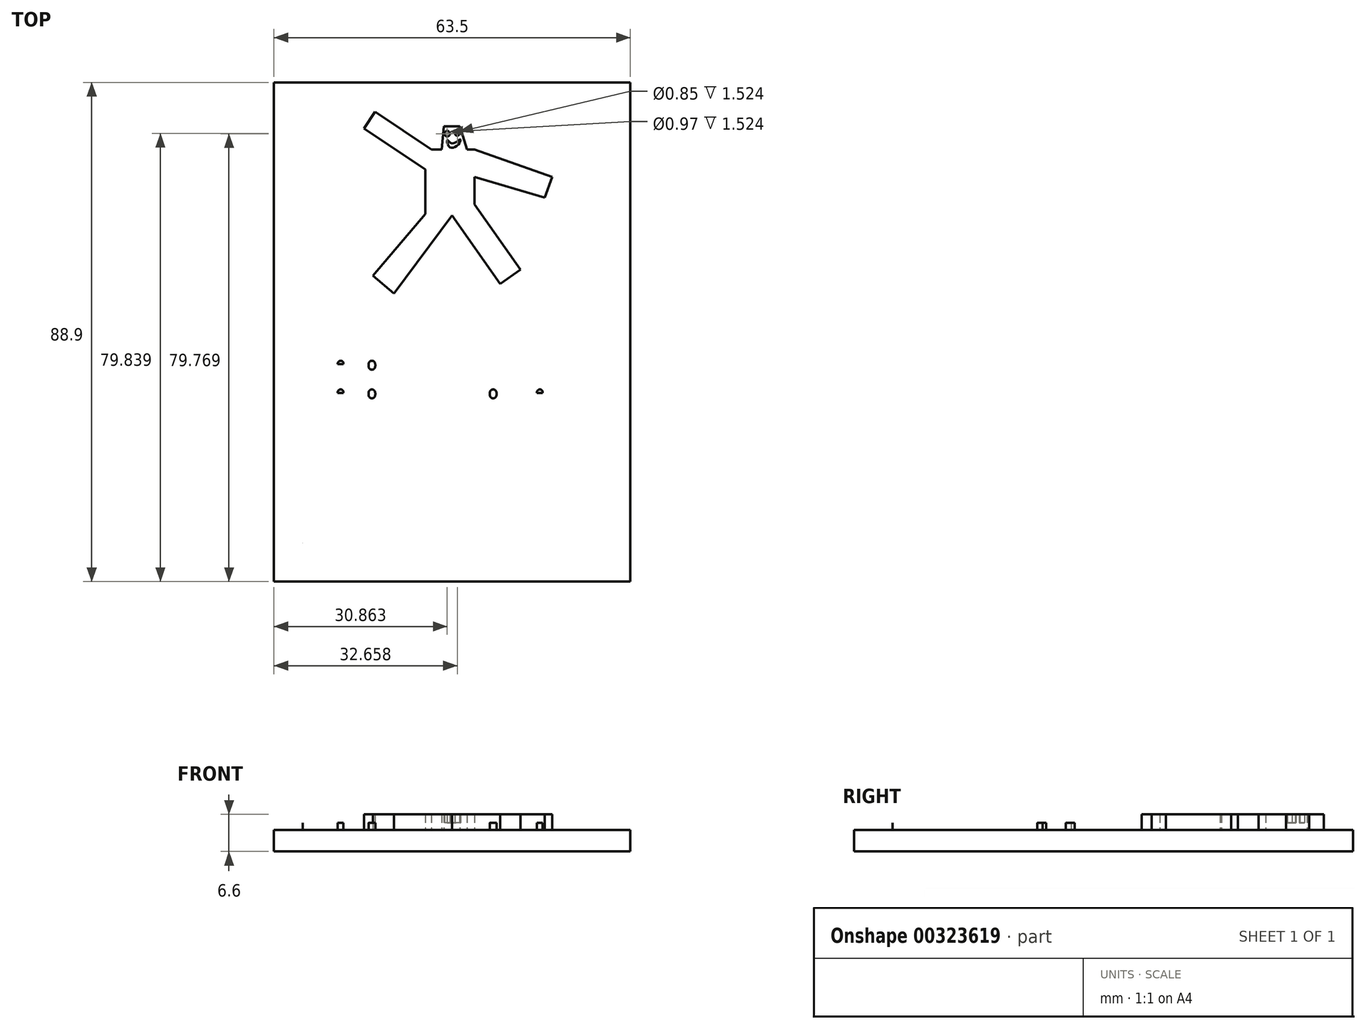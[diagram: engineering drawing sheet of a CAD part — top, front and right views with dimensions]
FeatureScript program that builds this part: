
annotation { "Feature Type Name" : "Feature", "Feature Type Description" : "" }
export const myFeature = defineFeature(function(context is Context, id is Id, definition is map)
    precondition{}
    {
        {
            var Q0;
            Q0=qCreatedBy(makeId("Top.planeOp"),FACE);
            var sketch = newSketch(context, id + "F0", { "sketchPlane" : qUnion([Q0])});
            skLineSegment(sketch, "E0.bottom", {"start": v(31.75, -44.45) * mm, "end": v(-31.75, -44.45) * mm});
            skLineSegment(sketch, "E0.top", {"start": v(31.75, 44.45) * mm, "end": v(-31.75, 44.45) * mm});
            skLineSegment(sketch, "E0.left", {"start": v(31.75, -44.45) * mm, "end": v(31.75, 44.45) * mm});
            skLineSegment(sketch, "E0.right", {"start": v(-31.75, -44.45) * mm, "end": v(-31.75, 44.45) * mm});
            skPoint(sketch, "E0.middle", {"position": v(0, 0) * mm});
            skSolve(sketch);
        }
        {
            var Q0;
            Q0=makeQuery(id+"F0.imprint","IMPRINT",FACE,{"disambiguationData":[TD([[makeQuery(id+"F0.imprint","IMPRINT",EDGE,{"derivedFrom":sQuery(id+"F0.wireOp",EDGE,"E0.bottom")}),-1.0]])]});
            extrude(context, id + "F1", {"entities" : qUnion([Q0]), "depth" : 5.08 * mm});
        }
        {
            var Q0;
            Q0=makeQuery(id+"F1.opExtrude","CAP_FACE",FACE,{"disambiguationData":[OSD([sQuery(id+"F0.wireOp",EDGE,"E0.bottom"),sQuery(id+"F0.wireOp",EDGE,"E0.top"),sQuery(id+"F0.wireOp",EDGE,"E0.left"),sQuery(id+"F0.wireOp",EDGE,"E0.right")])],"isStart":false});
            var sketch = newSketch(context, id + "F2", { "sketchPlane" : qUnion([Q0])});
            skLineSegment(sketch, "E1", {"start": v(0, 20.73) * mm, "end": v(8.52, 8.58) * mm});
            skLineSegment(sketch, "E2", {"start": v(8.52, 8.58) * mm, "end": v(12.15, 11.12) * mm});
            skLineSegment(sketch, "E3", {"start": v(12.15, 11.12) * mm, "end": v(4, 22.73) * mm});
            skLineSegment(sketch, "E4", {"start": v(4, 22.73) * mm, "end": v(4, 32.53) * mm});
            skLineSegment(sketch, "E5", {"start": v(4, 32.53) * mm, "end": v(0, 32.53) * mm});
            skLineSegment(sketch, "E6", {"start": v(0, 32.53) * mm, "end": v(-3.7, 32.53) * mm});
            skLineSegment(sketch, "E7", {"start": v(-3.7, 32.53) * mm, "end": v(-13.72, 39.26) * mm});
            skLineSegment(sketch, "E8", {"start": v(-13.72, 39.26) * mm, "end": v(-15.73, 36.26) * mm});
            skLineSegment(sketch, "E9", {"start": v(-15.73, 36.26) * mm, "end": v(-4.8, 28.92) * mm});
            skLineSegment(sketch, "E10", {"start": v(-4.8, 28.92) * mm, "end": v(-4.8, 21) * mm});
            skLineSegment(sketch, "E11", {"start": v(-4.8, 21) * mm, "end": v(-14.13, 10.02) * mm});
            skLineSegment(sketch, "E12", {"start": v(-14.13, 10.02) * mm, "end": v(-10.37, 6.82) * mm});
            skLineSegment(sketch, "E13", {"start": v(-10.37, 6.82) * mm, "end": v(0, 20.73) * mm});
            skLineSegment(sketch, "E14", {"start": v(4, 32.53) * mm, "end": v(17.8, 27.63) * mm});
            skPoint(sketch, "E14.endSnap0", {"position": v(4, 27.63) * mm});
            skLineSegment(sketch, "E15", {"start": v(17.8, 27.63) * mm, "end": v(16.49, 23.96) * mm});
            skLineSegment(sketch, "E16", {"start": v(16.49, 23.96) * mm, "end": v(4, 27.63) * mm});
            skLineSegment(sketch, "E17", {"start": v(-1.85, 32.53) * mm, "end": v(-1.48, 36.6) * mm});
            skLineSegment(sketch, "E18", {"start": v(-1.48, 36.6) * mm, "end": v(0, 36.6) * mm});
            skLineSegment(sketch, "E19", {"start": v(0, 36.6) * mm, "end": v(1.4, 36.6) * mm});
            skLineSegment(sketch, "E20", {"start": v(1.4, 36.6) * mm, "end": v(2.62, 32.53) * mm});
            skCircle(sketch, "E21", {"center": v(-0.89, 35.32) * mm, "radius": 0.48 * mm});
            skCircle(sketch, "E22", {"center": v(0.9, 35.39) * mm, "radius": 0.42 * mm});
            skFitSpline(sketch, "E23", {"points": [v(-0.85, 34.16) * mm, v(0, 33.57) * mm, v(1.45, 34.3) * mm, v(0.9, 33.2) * mm, v(-0.56, 33.01) * mm, v(-0.85, 34.16) * mm]});
            skText(sketch, "E24", { "text": "servo, jimmy:\nservo jimmy is worthless.    \n                                            1/1", "fontName": "OpenSans-Regular.ttf"});
            const initialGuessF2  = {"E24": [-0.02274, -0.00693, 1, 0, 0.0027]};
            skSetInitialGuess(sketch, initialGuessF2);
            skSolve(sketch);
        }
        {
            var Q0;
            Q0=makeQuery(id+"F2.imprint","IMPRINT",FACE,{"disambiguationData":[TD([[makeQuery(id+"F2.imprint","IMPRINT",EDGE,{"derivedFrom":sQuery(id+"F2.wireOp",EDGE,"E24.sketch_text.stroke-0")}),-1.0]])]});
            var Q1;
            Q1=makeQuery(id+"F2.imprint","IMPRINT",FACE,{"disambiguationData":[TD([[makeQuery(id+"F2.imprint","IMPRINT",EDGE,{"derivedFrom":sQuery(id+"F2.wireOp",EDGE,"E24.sketch_text.stroke-25")}),-1.0]])]});
            var Q2;
            Q2=makeQuery(id+"F2.imprint","IMPRINT",FACE,{"disambiguationData":[TD([[makeQuery(id+"F2.imprint","IMPRINT",EDGE,{"derivedFrom":sQuery(id+"F2.wireOp",EDGE,"E24.sketch_text.stroke-44")}),-1.0]])]});
            var Q3;
            Q3=makeQuery(id+"F2.imprint","IMPRINT",FACE,{"disambiguationData":[TD([[makeQuery(id+"F2.imprint","IMPRINT",EDGE,{"derivedFrom":sQuery(id+"F2.wireOp",EDGE,"E24.sketch_text.stroke-57")}),-1.0]])]});
            var Q4;
            Q4=makeQuery(id+"F2.imprint","IMPRINT",FACE,{"disambiguationData":[TD([[makeQuery(id+"F2.imprint","IMPRINT",EDGE,{"derivedFrom":sQuery(id+"F2.wireOp",EDGE,"E24.sketch_text.stroke-67")}),-1.0]])]});
            var Q5;
            Q5=makeQuery(id+"F2.imprint","IMPRINT",FACE,{"disambiguationData":[TD([[makeQuery(id+"F2.imprint","IMPRINT",EDGE,{"derivedFrom":sQuery(id+"F2.wireOp",EDGE,"E24.sketch_text.stroke-84")}),-1.0]])]});
            var Q6;
            Q6=makeQuery(id+"F2.imprint","IMPRINT",FACE,{"disambiguationData":[TD([[makeQuery(id+"F2.imprint","IMPRINT",EDGE,{"derivedFrom":sQuery(id+"F2.wireOp",EDGE,"E24.sketch_text.stroke-91")}),-1.0]])]});
            var Q7;
            Q7=makeQuery(id+"F2.imprint","IMPRINT",FACE,{"disambiguationData":[TD([[makeQuery(id+"F2.imprint","IMPRINT",EDGE,{"derivedFrom":sQuery(id+"F2.wireOp",EDGE,"E24.sketch_text.stroke-100")}),-1.0]])]});
            var Q8;
            Q8=makeQuery(id+"F2.imprint","IMPRINT",FACE,{"disambiguationData":[TD([[makeQuery(id+"F2.imprint","IMPRINT",EDGE,{"derivedFrom":sQuery(id+"F2.wireOp",EDGE,"E24.sketch_text.stroke-112")}),-1.0]])]});
            var Q9;
            Q9=makeQuery(id+"F2.imprint","IMPRINT",FACE,{"disambiguationData":[TD([[makeQuery(id+"F2.imprint","IMPRINT",EDGE,{"derivedFrom":sQuery(id+"F2.wireOp",EDGE,"E24.sketch_text.stroke-108")}),-1.0]])]});
            var Q10;
            Q10=makeQuery(id+"F2.imprint","IMPRINT",FACE,{"disambiguationData":[TD([[makeQuery(id+"F2.imprint","IMPRINT",EDGE,{"derivedFrom":sQuery(id+"F2.wireOp",EDGE,"E24.sketch_text.stroke-120")}),-1.0]])]});
            var Q11;
            Q11=makeQuery(id+"F2.imprint","IMPRINT",FACE,{"disambiguationData":[TD([[makeQuery(id+"F2.imprint","IMPRINT",EDGE,{"derivedFrom":sQuery(id+"F2.wireOp",EDGE,"E24.sketch_text.stroke-148")}),-1.0]])]});
            var Q12;
            Q12=makeQuery(id+"F2.imprint","IMPRINT",FACE,{"disambiguationData":[TD([[makeQuery(id+"F2.imprint","IMPRINT",EDGE,{"derivedFrom":sQuery(id+"F2.wireOp",EDGE,"E24.sketch_text.stroke-176")}),-1.0]])]});
            var Q13;
            Q13=makeQuery(id+"F2.imprint","IMPRINT",FACE,{"disambiguationData":[TD([[makeQuery(id+"F2.imprint","IMPRINT",EDGE,{"derivedFrom":sQuery(id+"F2.wireOp",EDGE,"E24.sketch_text.stroke-200")}),-1.0]])]});
            var Q14;
            Q14=makeQuery(id+"F2.imprint","IMPRINT",FACE,{"disambiguationData":[TD([[makeQuery(id+"F2.imprint","IMPRINT",EDGE,{"derivedFrom":sQuery(id+"F2.wireOp",EDGE,"E24.sketch_text.stroke-192")}),-1.0]])]});
            var Q15;
            Q15=makeQuery(id+"F2.imprint","IMPRINT",FACE,{"disambiguationData":[TD([[makeQuery(id+"F2.imprint","IMPRINT",EDGE,{"derivedFrom":sQuery(id+"F2.wireOp",EDGE,"E24.sketch_text.stroke-206")}),-1.0]])]});
            var Q16;
            Q16=makeQuery(id+"F2.imprint","IMPRINT",FACE,{"disambiguationData":[TD([[makeQuery(id+"F2.imprint","IMPRINT",EDGE,{"derivedFrom":sQuery(id+"F2.wireOp",EDGE,"E24.sketch_text.stroke-231")}),-1.0]])]});
            var Q17;
            Q17=makeQuery(id+"F2.imprint","IMPRINT",FACE,{"disambiguationData":[TD([[makeQuery(id+"F2.imprint","IMPRINT",EDGE,{"derivedFrom":sQuery(id+"F2.wireOp",EDGE,"E24.sketch_text.stroke-250")}),-1.0]])]});
            var Q18;
            Q18=makeQuery(id+"F2.imprint","IMPRINT",FACE,{"disambiguationData":[TD([[makeQuery(id+"F2.imprint","IMPRINT",EDGE,{"derivedFrom":sQuery(id+"F2.wireOp",EDGE,"E24.sketch_text.stroke-263")}),-1.0]])]});
            var Q19;
            Q19=makeQuery(id+"F2.imprint","IMPRINT",FACE,{"disambiguationData":[TD([[makeQuery(id+"F2.imprint","IMPRINT",EDGE,{"derivedFrom":sQuery(id+"F2.wireOp",EDGE,"E24.sketch_text.stroke-273")}),-1.0]])]});
            var Q20;
            Q20=makeQuery(id+"F2.imprint","IMPRINT",FACE,{"disambiguationData":[TD([[makeQuery(id+"F2.imprint","IMPRINT",EDGE,{"derivedFrom":sQuery(id+"F2.wireOp",EDGE,"E24.sketch_text.stroke-290")}),-1.0]])]});
            var Q21;
            Q21=makeQuery(id+"F2.imprint","IMPRINT",FACE,{"disambiguationData":[TD([[makeQuery(id+"F2.imprint","IMPRINT",EDGE,{"derivedFrom":sQuery(id+"F2.wireOp",EDGE,"E24.sketch_text.stroke-311")}),-1.0]])]});
            var Q22;
            Q22=makeQuery(id+"F2.imprint","IMPRINT",FACE,{"disambiguationData":[TD([[makeQuery(id+"F2.imprint","IMPRINT",EDGE,{"derivedFrom":sQuery(id+"F2.wireOp",EDGE,"E24.sketch_text.stroke-299")}),-1.0]])]});
            var Q23;
            Q23=makeQuery(id+"F2.imprint","IMPRINT",FACE,{"disambiguationData":[TD([[makeQuery(id+"F2.imprint","IMPRINT",EDGE,{"derivedFrom":sQuery(id+"F2.wireOp",EDGE,"E24.sketch_text.stroke-319")}),-1.0]])]});
            var Q24;
            Q24=makeQuery(id+"F2.imprint","IMPRINT",FACE,{"disambiguationData":[TD([[makeQuery(id+"F2.imprint","IMPRINT",EDGE,{"derivedFrom":sQuery(id+"F2.wireOp",EDGE,"E24.sketch_text.stroke-307")}),-1.0]])]});
            var Q25;
            Q25=makeQuery(id+"F2.imprint","IMPRINT",FACE,{"disambiguationData":[TD([[makeQuery(id+"F2.imprint","IMPRINT",EDGE,{"derivedFrom":sQuery(id+"F2.wireOp",EDGE,"E24.sketch_text.stroke-395")}),-1.0]])]});
            var Q26;
            Q26=makeQuery(id+"F2.imprint","IMPRINT",FACE,{"disambiguationData":[TD([[makeQuery(id+"F2.imprint","IMPRINT",EDGE,{"derivedFrom":sQuery(id+"F2.wireOp",EDGE,"E24.sketch_text.stroke-403")}),-1.0]])]});
            var Q27;
            Q27=makeQuery(id+"F2.imprint","IMPRINT",FACE,{"disambiguationData":[TD([[makeQuery(id+"F2.imprint","IMPRINT",EDGE,{"derivedFrom":sQuery(id+"F2.wireOp",EDGE,"E24.sketch_text.stroke-391")}),-1.0]])]});
            var Q28;
            Q28=makeQuery(id+"F2.imprint","IMPRINT",FACE,{"disambiguationData":[TD([[makeQuery(id+"F2.imprint","IMPRINT",EDGE,{"derivedFrom":sQuery(id+"F2.wireOp",EDGE,"E24.sketch_text.stroke-347")}),-1.0]])]});
            var Q29;
            Q29=makeQuery(id+"F2.imprint","IMPRINT",FACE,{"disambiguationData":[TD([[makeQuery(id+"F2.imprint","IMPRINT",EDGE,{"derivedFrom":sQuery(id+"F2.wireOp",EDGE,"E24.sketch_text.stroke-375")}),-1.0]])]});
            var Q30;
            Q30=makeQuery(id+"F2.imprint","IMPRINT",FACE,{"disambiguationData":[TD([[makeQuery(id+"F2.imprint","IMPRINT",EDGE,{"derivedFrom":sQuery(id+"F2.wireOp",EDGE,"E24.sketch_text.stroke-451")}),-1.0]])]});
            var Q31;
            Q31=makeQuery(id+"F2.imprint","IMPRINT",FACE,{"disambiguationData":[TD([[makeQuery(id+"F2.imprint","IMPRINT",EDGE,{"derivedFrom":sQuery(id+"F2.wireOp",EDGE,"E24.sketch_text.stroke-428")}),-1.0]])]});
            var Q32;
            Q32=makeQuery(id+"F2.imprint","IMPRINT",FACE,{"disambiguationData":[TD([[makeQuery(id+"F2.imprint","IMPRINT",EDGE,{"derivedFrom":sQuery(id+"F2.wireOp",EDGE,"E24.sketch_text.stroke-468")}),-1.0]])]});
            var Q33;
            Q33=makeQuery(id+"F2.imprint","IMPRINT",FACE,{"disambiguationData":[TD([[makeQuery(id+"F2.imprint","IMPRINT",EDGE,{"derivedFrom":sQuery(id+"F2.wireOp",EDGE,"E24.sketch_text.stroke-481")}),-1.0]])]});
            var Q34;
            Q34=makeQuery(id+"F2.imprint","IMPRINT",FACE,{"disambiguationData":[TD([[makeQuery(id+"F2.imprint","IMPRINT",EDGE,{"derivedFrom":sQuery(id+"F2.wireOp",EDGE,"E24.sketch_text.stroke-500")}),-1.0]])]});
            var Q35;
            Q35=makeQuery(id+"F2.imprint","IMPRINT",FACE,{"disambiguationData":[TD([[makeQuery(id+"F2.imprint","IMPRINT",EDGE,{"derivedFrom":sQuery(id+"F2.wireOp",EDGE,"E24.sketch_text.stroke-518")}),-1.0]])]});
            var Q36;
            Q36=makeQuery(id+"F2.imprint","IMPRINT",FACE,{"disambiguationData":[TD([[makeQuery(id+"F2.imprint","IMPRINT",EDGE,{"derivedFrom":sQuery(id+"F2.wireOp",EDGE,"E24.sketch_text.stroke-522")}),-1.0]])]});
            var Q37;
            Q37=makeQuery(id+"F2.imprint","IMPRINT",FACE,{"disambiguationData":[TD([[makeQuery(id+"F2.imprint","IMPRINT",EDGE,{"derivedFrom":sQuery(id+"F2.wireOp",EDGE,"E24.sketch_text.stroke-541")}),-1.0]])]});
            var Q38;
            Q38=makeQuery(id+"F2.imprint","IMPRINT",FACE,{"disambiguationData":[TD([[makeQuery(id+"F2.imprint","IMPRINT",EDGE,{"derivedFrom":sQuery(id+"F2.wireOp",EDGE,"E24.sketch_text.stroke-566")}),-1.0]])]});
            var Q39;
            Q39=makeQuery(id+"F2.imprint","IMPRINT",FACE,{"disambiguationData":[TD([[makeQuery(id+"F2.imprint","IMPRINT",EDGE,{"derivedFrom":sQuery(id+"F2.wireOp",EDGE,"E24.sketch_text.stroke-599")}),-1.0]])]});
            var Q40;
            Q40=makeQuery(id+"F2.imprint","IMPRINT",FACE,{"disambiguationData":[TD([[makeQuery(id+"F2.imprint","IMPRINT",EDGE,{"derivedFrom":sQuery(id+"F2.wireOp",EDGE,"E24.sketch_text.stroke-608")}),-1.0]])]});
            var Q41;
            Q41=makeQuery(id+"F2.imprint","IMPRINT",FACE,{"disambiguationData":[TD([[makeQuery(id+"F2.imprint","IMPRINT",EDGE,{"derivedFrom":sQuery(id+"F2.wireOp",EDGE,"E24.sketch_text.stroke-612")}),-1.0]])]});
            var Q42;
            Q42=makeQuery(id+"F2.imprint","IMPRINT",FACE,{"disambiguationData":[TD([[makeQuery(id+"F2.imprint","IMPRINT",EDGE,{"derivedFrom":sQuery(id+"F2.wireOp",EDGE,"E24.sketch_text.stroke-591")}),-1.0]])]});
            extrude(context, id + "F3", {"entities" : qUnion([Q0, Q1, Q2, Q3, Q4, Q5, Q6, Q7, Q8, Q9, Q10, Q11, Q12, Q13, Q14, Q15, Q16, Q17, Q18, Q19, Q20, Q21, Q22, Q23, Q24, Q25, Q26, Q27, Q28, Q29, Q30, Q31, Q32, Q33, Q34, Q35, Q36, Q37, Q38, Q39, Q40, Q41, Q42]), "operationType" : NewBodyOperationType.REMOVE, "oppositeDirection" : true, "depth" : 1.27 * mm});
        }
        {
            var Q0;
            Q0=makeQuery(id+"F2.imprint","IMPRINT",FACE,{"disambiguationData":[TD([[makeQuery(id+"F2.imprint","IMPRINT",EDGE,{"derivedFrom":sQuery(id+"F2.wireOp",EDGE,"E1")}),1.0]])]});
            var Q1;
            {var subQ0=sQuery(id+"F2.wireOp",EDGE,"E14");Q1=makeQuery(id+"F2.imprint","IMPRINT",FACE,{"disambiguationData":[TD([[makeQuery(id+"F2.imprint","IMPRINT",EDGE,{"derivedFrom":subQ0}),-1.0]])]});}
            var Q2;
            {var subQ0=sQuery(id+"F2.wireOp",EDGE,"E17");Q2=makeQuery(id+"F2.imprint","IMPRINT",FACE,{"disambiguationData":[TD([[makeQuery(id+"F2.imprint","IMPRINT",EDGE,{"derivedFrom":subQ0}),-1.0]])]});}
            extrude(context, id + "F4", {"entities" : qUnion([Q0, Q1, Q2]), "operationType" : NewBodyOperationType.ADD, "depth" : 1.52 * mm});
        }
        {
            var Q0;
            Q0=makeQuery(id+"F2.imprint","IMPRINT",FACE,{"disambiguationData":[TD([[makeQuery(id+"F2.imprint","IMPRINT",EDGE,{"derivedFrom":sQuery(id+"F2.wireOp",EDGE,"E1")}),-1.0]])]});
            var sketch = newSketch(context, id + "F5", { "sketchPlane" : qUnion([Q0])});
            skFitSpline(sketch, "E25", {"points": [v(-26.28, -37.6) * mm, v(-24.66, -36.24) * mm, v(-26, -34.84) * mm, v(-27.95, -36.5) * mm, v(-26.28, -37.6) * mm]});
            skFitSpline(sketch, "E26", {"points": [v(-26.28, -37.6) * mm, v(-24.66, -37.6) * mm, v(-24.66, -38.83) * mm, v(-26.28, -39.8) * mm, v(-27.48, -38.6) * mm, v(-26.28, -37.6) * mm]});
            skLineSegment(sketch, "E27", {"start": v(-26.68, -33.27) * mm, "end": v(-25.12, -41.42) * mm});
            skLineSegment(sketch, "E28", {"start": v(-28.77, -38.13) * mm, "end": v(-22.3, -36.5) * mm});
            skLineSegment(sketch, "E29.bottom", {"start": v(-22.3, -37.31) * mm, "end": v(-30.26, -37.31) * mm});
            skLineSegment(sketch, "E29.top", {"start": v(-22.3, -37.89) * mm, "end": v(-30.26, -37.89) * mm});
            skLineSegment(sketch, "E29.left", {"start": v(-22.3, -37.31) * mm, "end": v(-22.3, -37.89) * mm});
            skLineSegment(sketch, "E29.right", {"start": v(-30.26, -37.31) * mm, "end": v(-30.26, -37.89) * mm});
            skPoint(sketch, "E29.cornerSnap0", {"position": v(-25.53, -37.31) * mm});
            skLineSegment(sketch, "E30.bottom", {"start": v(-25.9, -42.16) * mm, "end": v(-26.65, -42.16) * mm});
            skLineSegment(sketch, "E30.top", {"start": v(-25.9, -33.04) * mm, "end": v(-26.65, -33.04) * mm});
            skLineSegment(sketch, "E30.left", {"start": v(-25.9, -42.16) * mm, "end": v(-25.9, -33.04) * mm});
            skLineSegment(sketch, "E30.right", {"start": v(-26.65, -42.16) * mm, "end": v(-26.65, -33.04) * mm});
            skPoint(sketch, "E30.cornerSnap0", {"position": v(-25.9, -37.34) * mm});
            skSolve(sketch);
        }
        {
            var Q0;
            {var subQ0=sQuery(id+"F5.wireOp",EDGE,"E29.left");Q0=makeQuery(id+"F5.imprint","IMPRINT",FACE,{"disambiguationData":[TD([[makeQuery(id+"F5.imprint","IMPRINT",EDGE,{"derivedFrom":subQ0}),-1.0]])]});}
            var Q1;
            {var subQ0=sQuery(id+"F5.wireOp",EDGE,"E29.right");Q1=makeQuery(id+"F5.imprint","IMPRINT",FACE,{"disambiguationData":[TD([[makeQuery(id+"F5.imprint","IMPRINT",EDGE,{"derivedFrom":subQ0}),1.0]])]});}
            var Q2;
            {var subQ0=sQuery(id+"F5.wireOp",EDGE,"E27");var subQ1=sQuery(id+"F5.wireOp",EDGE,"E25");var subQ2=makeQuery(id+"F5.imprint","INTERSECT",VERTEX,{"disambiguationData":[OD(0.0)],"derivedFrom":[subQ1,subQ0]});Q2=makeQuery(id+"F5.imprint","IMPRINT",FACE,{"disambiguationData":[TD([[makeQuery(id+"F5.imprint","IMPRINT",EDGE,{"disambiguationData":[TD([[subQ2,-1.0]])],"derivedFrom":subQ1}),-1.0]])]});}
            var Q3;
            {var subQ0=sQuery(id+"F5.wireOp",EDGE,"E30.left");var subQ1=sQuery(id+"F5.wireOp",EDGE,"E25");var subQ2=makeQuery(id+"F5.imprint","INTERSECT",VERTEX,{"disambiguationData":[OD(0.0)],"derivedFrom":[subQ1,subQ0]});Q3=makeQuery(id+"F5.imprint","IMPRINT",FACE,{"disambiguationData":[TD([[makeQuery(id+"F5.imprint","IMPRINT",EDGE,{"disambiguationData":[TD([[subQ2,1.0]])],"derivedFrom":subQ1}),-1.0]])]});}
            var Q4;
            {var subQ0=sQuery(id+"F5.wireOp",EDGE,"E30.left");var subQ1=sQuery(id+"F5.wireOp",EDGE,"E25");var subQ2=makeQuery(id+"F5.imprint","INTERSECT",VERTEX,{"disambiguationData":[OD(0.0)],"derivedFrom":[subQ1,subQ0]});Q4=makeQuery(id+"F5.imprint","IMPRINT",FACE,{"disambiguationData":[TD([[makeQuery(id+"F5.imprint","IMPRINT",EDGE,{"disambiguationData":[TD([[subQ2,-1.0]])],"derivedFrom":subQ1}),-1.0]])]});}
            var Q5;
            {var subQ0=sQuery(id+"F5.wireOp",EDGE,"E29.top");var subQ1=sQuery(id+"F5.wireOp",EDGE,"E26");var subQ2=makeQuery(id+"F5.imprint","INTERSECT",VERTEX,{"disambiguationData":[OD(1.0)],"derivedFrom":[subQ1,subQ0]});Q5=makeQuery(id+"F5.imprint","IMPRINT",FACE,{"disambiguationData":[TD([[makeQuery(id+"F5.imprint","IMPRINT",EDGE,{"disambiguationData":[TD([[subQ2,-1.0]])],"derivedFrom":subQ1}),-1.0]])]});}
            var Q6;
            {var subQ0=sQuery(id+"F5.wireOp",EDGE,"E29.top");var subQ1=sQuery(id+"F5.wireOp",EDGE,"E26");var subQ2=makeQuery(id+"F5.imprint","INTERSECT",VERTEX,{"disambiguationData":[OD(1.0)],"derivedFrom":[subQ1,subQ0]});Q6=makeQuery(id+"F5.imprint","IMPRINT",FACE,{"disambiguationData":[TD([[makeQuery(id+"F5.imprint","IMPRINT",EDGE,{"disambiguationData":[TD([[subQ2,-1.0]])],"derivedFrom":subQ1}),1.0]])]});}
            var Q7;
            {var subQ0=sQuery(id+"F5.wireOp",EDGE,"E26");var subQ1=sQuery(id+"F5.wireOp",EDGE,"E25");var subQ2=makeQuery(id+"F5.imprint","INTERSECT",VERTEX,{"disambiguationData":[OD(0.0)],"derivedFrom":[subQ1,subQ0]});Q7=makeQuery(id+"F5.imprint","IMPRINT",FACE,{"disambiguationData":[TD([[makeQuery(id+"F5.imprint","IMPRINT",EDGE,{"disambiguationData":[TD([[subQ2,1.0]])],"derivedFrom":subQ1}),-1.0]])]});}
            var Q8;
            {var subQ0=sQuery(id+"F5.wireOp",EDGE,"E26");var subQ1=sQuery(id+"F5.wireOp",EDGE,"E25");var subQ2=makeQuery(id+"F5.imprint","INTERSECT",VERTEX,{"disambiguationData":[OD(0.0)],"derivedFrom":[subQ1,subQ0]});Q8=makeQuery(id+"F5.imprint","IMPRINT",FACE,{"disambiguationData":[TD([[makeQuery(id+"F5.imprint","IMPRINT",EDGE,{"disambiguationData":[TD([[subQ2,1.0]])],"derivedFrom":subQ1}),1.0]])]});}
            var Q9;
            {var subQ0=sQuery(id+"F5.wireOp",EDGE,"E30.left");var subQ1=sQuery(id+"F5.wireOp",EDGE,"E25");var subQ2=makeQuery(id+"F5.imprint","INTERSECT",VERTEX,{"disambiguationData":[OD(0.0)],"derivedFrom":[subQ1,subQ0]});Q9=makeQuery(id+"F5.imprint","IMPRINT",FACE,{"disambiguationData":[TD([[makeQuery(id+"F5.imprint","IMPRINT",EDGE,{"disambiguationData":[TD([[subQ2,1.0]])],"derivedFrom":subQ1}),1.0]])]});}
            var Q10;
            {var subQ1=sQuery(id+"F5.wireOp",EDGE,"E26");var subQ6=sQuery(id+"F5.wireOp",EDGE,"E25");var subQ9=makeQuery(id+"F5.imprint","INTERSECT",VERTEX,{"disambiguationData":[OD(1.0)],"derivedFrom":[subQ6,subQ1]});Q10=makeQuery(id+"F5.imprint","IMPRINT",FACE,{"disambiguationData":[TD([[makeQuery(id+"F5.imprint","IMPRINT",EDGE,{"disambiguationData":[TD([[subQ9,-1.0]])],"derivedFrom":subQ6}),1.0]])]});}
            var Q11;
            {var subQ0=sQuery(id+"F5.wireOp",EDGE,"E30.left");var subQ1=sQuery(id+"F5.wireOp",EDGE,"E26");var subQ2=makeQuery(id+"F5.imprint","INTERSECT",VERTEX,{"disambiguationData":[OD(0.0)],"derivedFrom":[subQ1,subQ0]});Q11=makeQuery(id+"F5.imprint","IMPRINT",FACE,{"disambiguationData":[TD([[makeQuery(id+"F5.imprint","IMPRINT",EDGE,{"disambiguationData":[TD([[subQ2,-1.0]])],"derivedFrom":subQ1}),1.0]])]});}
            var Q12;
            {var subQ0=sQuery(id+"F5.wireOp",EDGE,"E27");var subQ1=sQuery(id+"F5.wireOp",EDGE,"E25");var subQ2=makeQuery(id+"F5.imprint","INTERSECT",VERTEX,{"disambiguationData":[OD(0.0)],"derivedFrom":[subQ1,subQ0]});Q12=makeQuery(id+"F5.imprint","IMPRINT",FACE,{"disambiguationData":[TD([[makeQuery(id+"F5.imprint","IMPRINT",EDGE,{"disambiguationData":[TD([[subQ2,-1.0]])],"derivedFrom":subQ1}),1.0]])]});}
            var Q13;
            {var subQ0=sQuery(id+"F5.wireOp",EDGE,"E30.left");var subQ1=sQuery(id+"F5.wireOp",EDGE,"E25");var subQ2=makeQuery(id+"F5.imprint","INTERSECT",VERTEX,{"disambiguationData":[OD(0.0)],"derivedFrom":[subQ1,subQ0]});Q13=makeQuery(id+"F5.imprint","IMPRINT",FACE,{"disambiguationData":[TD([[makeQuery(id+"F5.imprint","IMPRINT",EDGE,{"disambiguationData":[TD([[subQ2,-1.0]])],"derivedFrom":subQ1}),1.0]])]});}
            var Q14;
            {var subQ0=sQuery(id+"F5.wireOp",EDGE,"E29.bottom");var subQ1=sQuery(id+"F5.wireOp",EDGE,"E25");var subQ2=makeQuery(id+"F5.imprint","INTERSECT",VERTEX,{"disambiguationData":[OD(1.0)],"derivedFrom":[subQ1,subQ0]});Q14=makeQuery(id+"F5.imprint","IMPRINT",FACE,{"disambiguationData":[TD([[makeQuery(id+"F5.imprint","IMPRINT",EDGE,{"disambiguationData":[TD([[subQ2,-1.0]])],"derivedFrom":subQ1}),1.0]])]});}
            var Q15;
            {var subQ0=sQuery(id+"F5.wireOp",EDGE,"E30.right");var subQ1=sQuery(id+"F5.wireOp",EDGE,"E25");var subQ2=makeQuery(id+"F5.imprint","INTERSECT",VERTEX,{"disambiguationData":[OD(1.0)],"derivedFrom":[subQ1,subQ0]});Q15=makeQuery(id+"F5.imprint","IMPRINT",FACE,{"disambiguationData":[TD([[makeQuery(id+"F5.imprint","IMPRINT",EDGE,{"disambiguationData":[TD([[subQ2,-1.0]])],"derivedFrom":subQ1}),-1.0]])]});}
            var Q16;
            {var subQ0=sQuery(id+"F5.wireOp",EDGE,"E30.left");var subQ1=sQuery(id+"F5.wireOp",EDGE,"E27");var subQ2=makeQuery(id+"F5.imprint","INTERSECT",VERTEX,{"derivedFrom":[subQ1,subQ0]});Q16=makeQuery(id+"F5.imprint","IMPRINT",FACE,{"disambiguationData":[TD([[makeQuery(id+"F5.imprint","IMPRINT",EDGE,{"disambiguationData":[TD([[subQ2,-1.0]])],"derivedFrom":subQ1}),1.0]])]});}
            var Q17;
            {var subQ0=sQuery(id+"F5.wireOp",EDGE,"E30.left");var subQ1=sQuery(id+"F5.wireOp",EDGE,"E27");var subQ2=makeQuery(id+"F5.imprint","INTERSECT",VERTEX,{"derivedFrom":[subQ1,subQ0]});Q17=makeQuery(id+"F5.imprint","IMPRINT",FACE,{"disambiguationData":[TD([[makeQuery(id+"F5.imprint","IMPRINT",EDGE,{"disambiguationData":[TD([[subQ2,-1.0]])],"derivedFrom":subQ1}),-1.0]])]});}
            var Q18;
            {var subQ1=sQuery(id+"F5.wireOp",EDGE,"E25");var subQ5=sQuery(id+"F5.wireOp",EDGE,"E30.right");var subQ6=makeQuery(id+"F5.imprint","INTERSECT",VERTEX,{"disambiguationData":[OD(1.0)],"derivedFrom":[subQ1,subQ5]});Q18=makeQuery(id+"F5.imprint","IMPRINT",FACE,{"disambiguationData":[TD([[makeQuery(id+"F5.imprint","IMPRINT",EDGE,{"disambiguationData":[TD([[subQ6,-1.0]])],"derivedFrom":subQ1}),1.0]])]});}
            var Q19;
            {var subQ0=sQuery(id+"F5.wireOp",EDGE,"E29.bottom");var subQ1=sQuery(id+"F5.wireOp",EDGE,"E27");var subQ2=makeQuery(id+"F5.imprint","INTERSECT",VERTEX,{"derivedFrom":[subQ1,subQ0]});Q19=makeQuery(id+"F5.imprint","IMPRINT",FACE,{"disambiguationData":[TD([[makeQuery(id+"F5.imprint","IMPRINT",EDGE,{"disambiguationData":[TD([[subQ2,-1.0]])],"derivedFrom":subQ1}),1.0]])]});}
            var Q20;
            {var subQ0=sQuery(id+"F5.wireOp",EDGE,"E30.top");Q20=makeQuery(id+"F5.imprint","IMPRINT",FACE,{"disambiguationData":[TD([[makeQuery(id+"F5.imprint","IMPRINT",EDGE,{"derivedFrom":subQ0}),1.0]])]});}
            var Q21;
            {var subQ0=sQuery(id+"F5.wireOp",EDGE,"E27");var subQ1=sQuery(id+"F5.wireOp",EDGE,"E25");var subQ2=makeQuery(id+"F5.imprint","INTERSECT",VERTEX,{"disambiguationData":[OD(1.0)],"derivedFrom":[subQ1,subQ0]});Q21=makeQuery(id+"F5.imprint","IMPRINT",FACE,{"disambiguationData":[TD([[makeQuery(id+"F5.imprint","IMPRINT",EDGE,{"disambiguationData":[TD([[subQ2,-1.0]])],"derivedFrom":subQ1}),-1.0]])]});}
            var Q22;
            {var subQ0=sQuery(id+"F5.wireOp",EDGE,"E30.left");var subQ1=sQuery(id+"F5.wireOp",EDGE,"E25");var subQ2=makeQuery(id+"F5.imprint","INTERSECT",VERTEX,{"disambiguationData":[OD(1.0)],"derivedFrom":[subQ1,subQ0]});Q22=makeQuery(id+"F5.imprint","IMPRINT",FACE,{"disambiguationData":[TD([[makeQuery(id+"F5.imprint","IMPRINT",EDGE,{"disambiguationData":[TD([[subQ2,-1.0]])],"derivedFrom":subQ1}),1.0]])]});}
            var Q23;
            {var subQ0=sQuery(id+"F5.wireOp",EDGE,"E27");var subQ1=sQuery(id+"F5.wireOp",EDGE,"E25");var subQ2=makeQuery(id+"F5.imprint","INTERSECT",VERTEX,{"disambiguationData":[OD(1.0)],"derivedFrom":[subQ1,subQ0]});Q23=makeQuery(id+"F5.imprint","IMPRINT",FACE,{"disambiguationData":[TD([[makeQuery(id+"F5.imprint","IMPRINT",EDGE,{"disambiguationData":[TD([[subQ2,-1.0]])],"derivedFrom":subQ1}),1.0]])]});}
            var Q24;
            {var subQ0=sQuery(id+"F5.wireOp",EDGE,"E30.left");var subQ1=sQuery(id+"F5.wireOp",EDGE,"E26");var subQ2=makeQuery(id+"F5.imprint","INTERSECT",VERTEX,{"disambiguationData":[OD(1.0)],"derivedFrom":[subQ1,subQ0]});Q24=makeQuery(id+"F5.imprint","IMPRINT",FACE,{"disambiguationData":[TD([[makeQuery(id+"F5.imprint","IMPRINT",EDGE,{"disambiguationData":[TD([[subQ2,-1.0]])],"derivedFrom":subQ1}),-1.0]])]});}
            var Q25;
            {var subQ5=sQuery(id+"F5.wireOp",EDGE,"E30.bottom");Q25=makeQuery(id+"F5.imprint","IMPRINT",FACE,{"disambiguationData":[TD([[makeQuery(id+"F5.imprint","IMPRINT",EDGE,{"derivedFrom":subQ5}),-1.0]])]});}
            var Q26;
            {var subQ0=sQuery(id+"F5.wireOp",EDGE,"E30.right");var subQ1=sQuery(id+"F5.wireOp",EDGE,"E26");var subQ2=makeQuery(id+"F5.imprint","INTERSECT",VERTEX,{"disambiguationData":[OD(0.0)],"derivedFrom":[subQ1,subQ0]});Q26=makeQuery(id+"F5.imprint","IMPRINT",FACE,{"disambiguationData":[TD([[makeQuery(id+"F5.imprint","IMPRINT",EDGE,{"disambiguationData":[TD([[subQ2,-1.0]])],"derivedFrom":subQ1}),-1.0]])]});}
            var Q27;
            {var subQ0=sQuery(id+"F5.wireOp",EDGE,"E27");var subQ1=sQuery(id+"F5.wireOp",EDGE,"E26");var subQ2=makeQuery(id+"F5.imprint","INTERSECT",VERTEX,{"disambiguationData":[OD(0.0)],"derivedFrom":[subQ1,subQ0]});Q27=makeQuery(id+"F5.imprint","IMPRINT",FACE,{"disambiguationData":[TD([[makeQuery(id+"F5.imprint","IMPRINT",EDGE,{"disambiguationData":[TD([[subQ2,-1.0]])],"derivedFrom":subQ1}),-1.0]])]});}
            var Q28;
            {var subQ0=sQuery(id+"F5.wireOp",EDGE,"E27");var subQ1=sQuery(id+"F5.wireOp",EDGE,"E26");var subQ2=makeQuery(id+"F5.imprint","INTERSECT",VERTEX,{"disambiguationData":[OD(0.0)],"derivedFrom":[subQ1,subQ0]});Q28=makeQuery(id+"F5.imprint","IMPRINT",FACE,{"disambiguationData":[TD([[makeQuery(id+"F5.imprint","IMPRINT",EDGE,{"disambiguationData":[TD([[subQ2,1.0]])],"derivedFrom":subQ1}),-1.0]])]});}
            var Q29;
            {var subQ0=sQuery(id+"F5.wireOp",EDGE,"E30.right");var subQ1=sQuery(id+"F5.wireOp",EDGE,"E25");var subQ2=makeQuery(id+"F5.imprint","INTERSECT",VERTEX,{"disambiguationData":[OD(0.0)],"derivedFrom":[subQ1,subQ0]});Q29=makeQuery(id+"F5.imprint","IMPRINT",FACE,{"disambiguationData":[TD([[makeQuery(id+"F5.imprint","IMPRINT",EDGE,{"disambiguationData":[TD([[subQ2,-1.0]])],"derivedFrom":subQ1}),1.0]])]});}
            var Q30;
            {var subQ0=sQuery(id+"F5.wireOp",EDGE,"E28");var subQ1=sQuery(id+"F5.wireOp",EDGE,"E25");var subQ2=makeQuery(id+"F5.imprint","INTERSECT",VERTEX,{"disambiguationData":[OD(0.0)],"derivedFrom":[subQ1,subQ0]});Q30=makeQuery(id+"F5.imprint","IMPRINT",FACE,{"disambiguationData":[TD([[makeQuery(id+"F5.imprint","IMPRINT",EDGE,{"disambiguationData":[TD([[subQ2,-1.0]])],"derivedFrom":subQ1}),1.0]])]});}
            var Q31;
            {var subQ0=sQuery(id+"F5.wireOp",EDGE,"E28");var subQ1=sQuery(id+"F5.wireOp",EDGE,"E25");var subQ2=makeQuery(id+"F5.imprint","INTERSECT",VERTEX,{"disambiguationData":[OD(0.0)],"derivedFrom":[subQ1,subQ0]});Q31=makeQuery(id+"F5.imprint","IMPRINT",FACE,{"disambiguationData":[TD([[makeQuery(id+"F5.imprint","IMPRINT",EDGE,{"disambiguationData":[TD([[subQ2,1.0]])],"derivedFrom":subQ1}),1.0]])]});}
            extrude(context, id + "F6", {"entities" : qUnion([Q0, Q1, Q2, Q3, Q4, Q5, Q6, Q7, Q8, Q9, Q10, Q11, Q12, Q13, Q14, Q15, Q16, Q17, Q18, Q19, Q20, Q21, Q22, Q23, Q24, Q25, Q26, Q27, Q28, Q29, Q30, Q31]), "operationType" : NewBodyOperationType.REMOVE, "oppositeDirection" : true, "depth" : 1.27 * mm});
        }
    });
